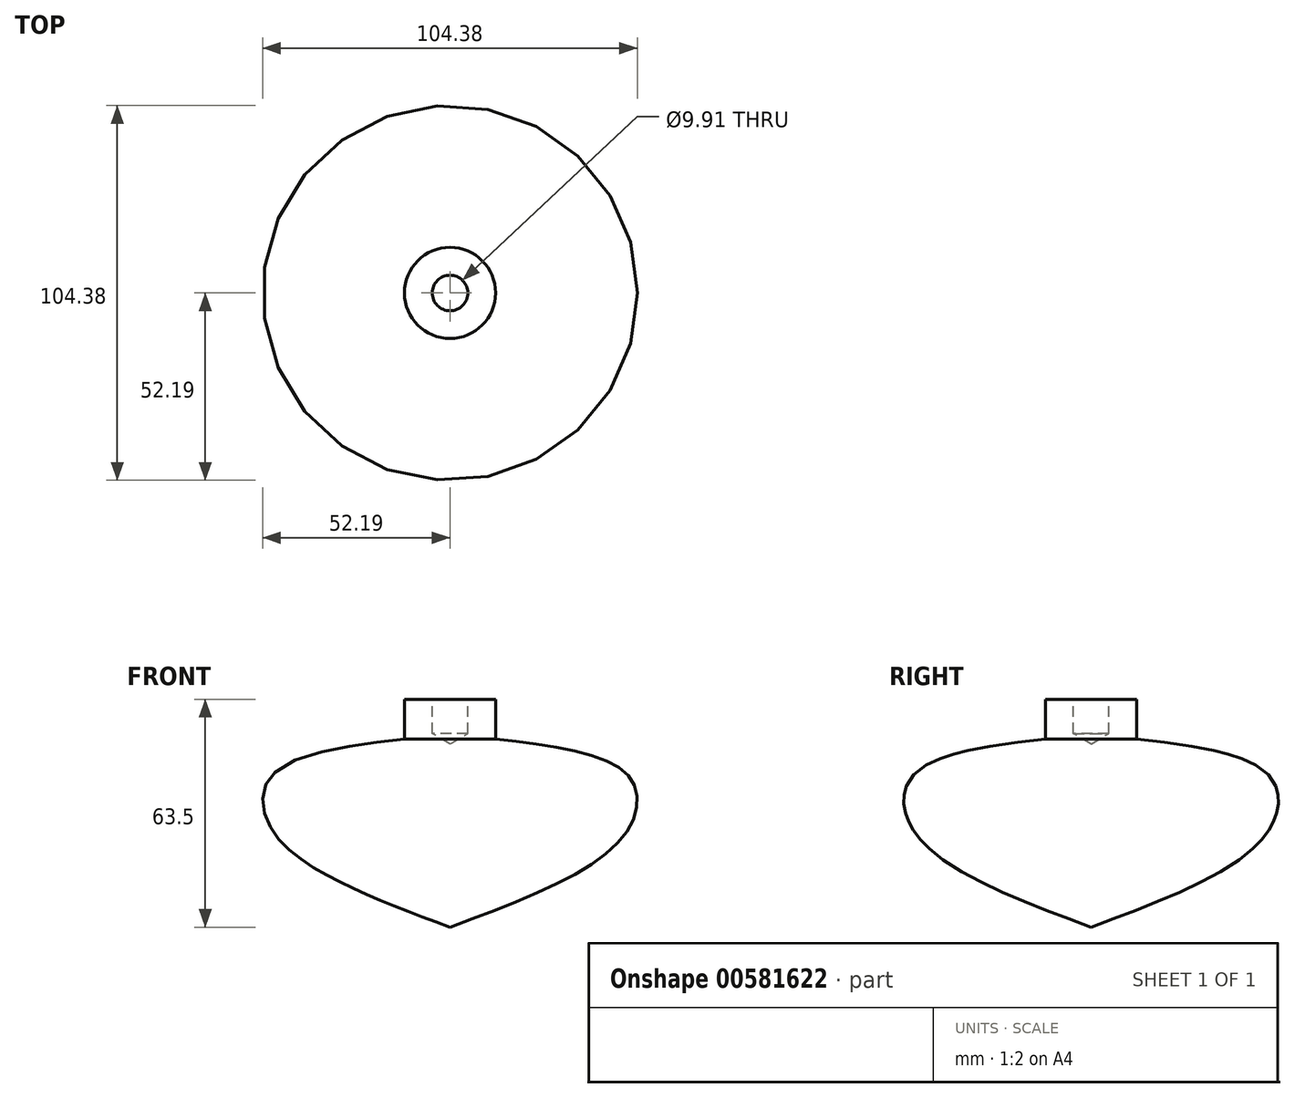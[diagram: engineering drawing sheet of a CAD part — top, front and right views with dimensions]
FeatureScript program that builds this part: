
annotation { "Feature Type Name" : "Feature", "Feature Type Description" : "" }
export const myFeature = defineFeature(function(context is Context, id is Id, definition is map)
    precondition{}
    {
        {
            var Q0;
            Q0=qCreatedBy(makeId("Front.planeOp"),FACE);
            var sketch = newSketch(context, id + "F0", { "sketchPlane" : qUnion([Q0])});
            skFitSpline(sketch, "E0", {"points": [v(0, 0) * mm, v(48.34, 25.33) * mm, v(49.77, 42.1) * mm, v(12.7, 52.44) * mm], "startDerivative": vector(144.28, 53.7) * mm, "endDerivative": vector(-131.68, 16) * mm});
            skLineSegment(sketch, "E1", {"start": v(12.7, 52.44) * mm, "end": v(12.7, 63.5) * mm});
            skLineSegment(sketch, "E2", {"start": v(12.7, 63.5) * mm, "end": v(0, 63.5) * mm});
            skLineSegment(sketch, "E3", {"start": v(0, 63.5) * mm, "end": v(0, 0) * mm});
            skSolve(sketch);
        }
        {
            var Q0;
            Q0=makeQuery(id+"F0.imprint","IMPRINT",FACE,{"disambiguationData":[TD([[makeQuery(id+"F0.imprint","IMPRINT",EDGE,{"derivedFrom":sQuery(id+"F0.wireOp",EDGE,"E0")}),1.0]])]});
            var Q1;
            Q1=sQuery(id+"F0.wireOp",EDGE,"E3");
            revolve(context, id + "F1", {"entities" : qUnion([Q0]), "axis" : qUnion([Q1]), "revolveType" : RevolveType.FULL});
        }
        {
            var Q0;
            Q0=makeQuery(id+"F1.opRevolve","SWEPT_FACE",FACE,{"disambiguationData":[OSD([sQuery(id+"F0.wireOp",EDGE,"E2")])]});
            var sketch = newSketch(context, id + "F2", { "sketchPlane" : qUnion([Q0])});
            skPoint(sketch, "E4", {"position": v(0, 0) * mm});
            skSolve(sketch);
        }
        {
            var Q0;
            Q0=sQuery(id+"F2.wireOp",VERTEX,"E4");
            var Q1;
            Q1=makeQuery(id+"F1.opRevolve","SWEPT_BODY",BODY,{"disambiguationData":[OSD([sQuery(id+"F0.wireOp",EDGE,"E0"),sQuery(id+"F0.wireOp",EDGE,"E1"),sQuery(id+"F0.wireOp",EDGE,"E2"),sQuery(id+"F0.wireOp",EDGE,"E3")])]});
            hole(context, id + "F3", {"style" : HoleStyle.SIMPLE, "endStyle" : HoleEndStyle.BLIND, "holeDiameter" : 9.9 * mm, "majorDiameter" : 6.35 * mm, "holeDepth" : 9.52 * mm, "isTappedThrough" : true, "tappedDepth" : 12.7 * mm, "tapClearance" : 3, "locations" : qUnion([Q0]), "scope" : qUnion([Q1])});
        }
    });
